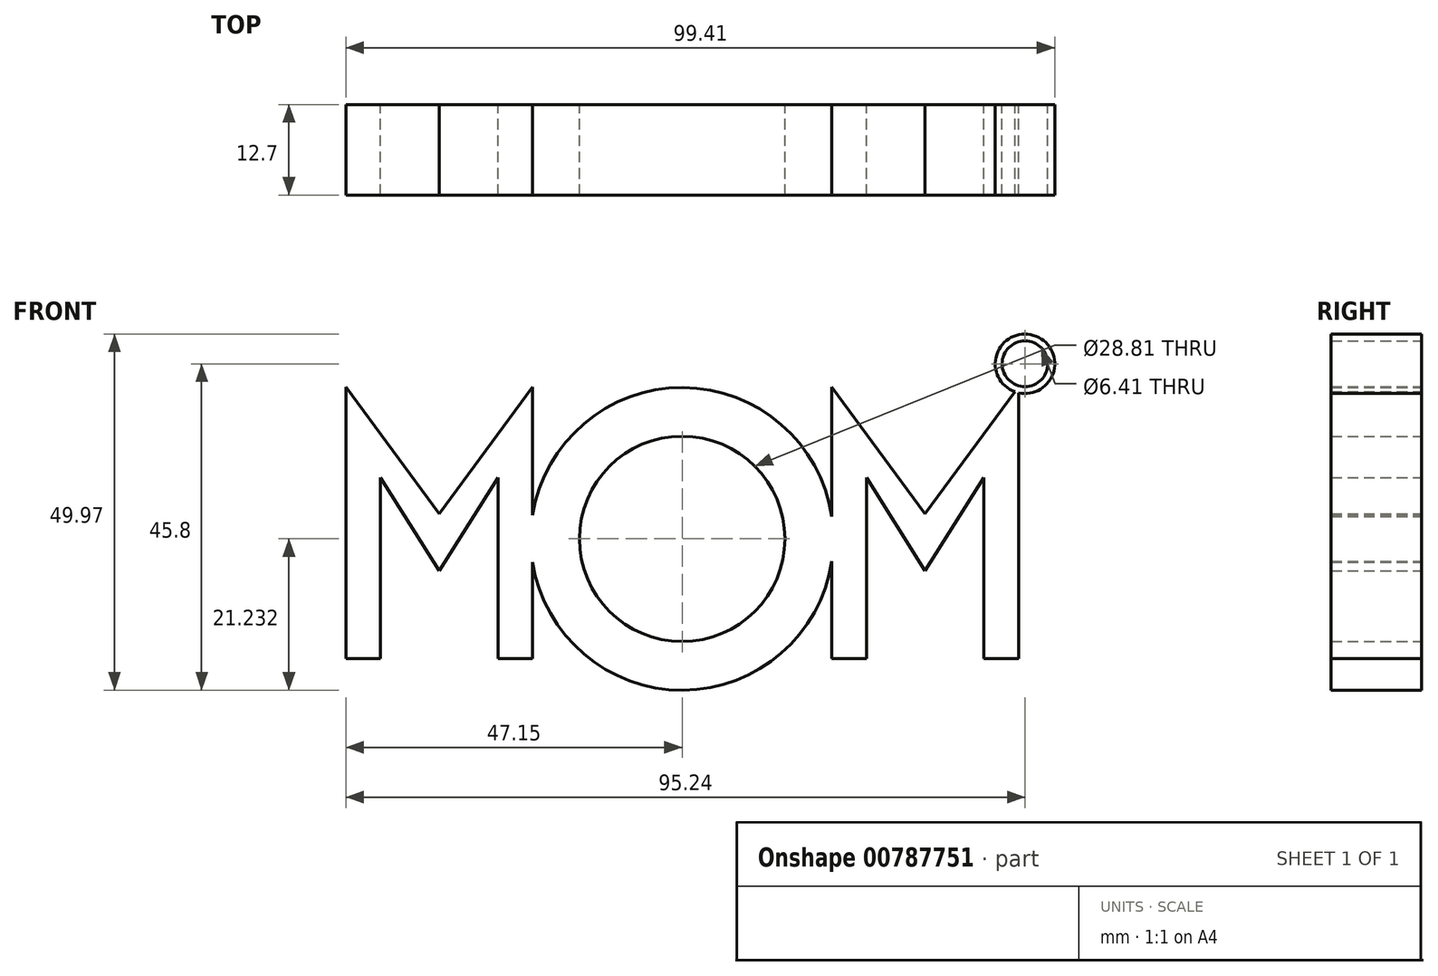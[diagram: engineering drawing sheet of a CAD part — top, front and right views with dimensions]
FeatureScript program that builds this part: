
annotation { "Feature Type Name" : "Feature", "Feature Type Description" : "" }
export const myFeature = defineFeature(function(context is Context, id is Id, definition is map)
    precondition{}
    {
        {
            var Q0;
            Q0=qCreatedBy(makeId("Front.planeOp"),FACE);
            var sketch = newSketch(context, id + "F0", { "sketchPlane" : qUnion([Q0])});
            skLineSegment(sketch, "E0", {"start": v(-42.31, -9.94) * mm, "end": v(-42.31, 15.46) * mm});
            skLineSegment(sketch, "E1", {"start": v(-42.31, 15.46) * mm, "end": v(-34.06, 2.34) * mm});
            skLineSegment(sketch, "E2", {"start": v(-34.06, 2.34) * mm, "end": v(-25.81, 15.46) * mm});
            skLineSegment(sketch, "E3", {"start": v(-25.81, 15.46) * mm, "end": v(-25.81, -9.94) * mm});
            skLineSegment(sketch, "E4", {"start": v(-42.31, -9.94) * mm, "end": v(-47.15, -9.94) * mm});
            skLineSegment(sketch, "E5", {"start": v(-47.15, -9.94) * mm, "end": v(-47.15, 28.16) * mm});
            skLineSegment(sketch, "E6", {"start": v(-47.15, 28.16) * mm, "end": v(-34.06, 10.35) * mm});
            skLineSegment(sketch, "E7", {"start": v(-34.06, 10.35) * mm, "end": v(-20.97, 28.16) * mm});
            skLineSegment(sketch, "E8", {"start": v(-20.97, 28.16) * mm, "end": v(-20.97, -9.94) * mm});
            skLineSegment(sketch, "E9", {"start": v(-20.97, -9.94) * mm, "end": v(-25.81, -9.94) * mm});
            skCircle(sketch, "E10", {"center": v(0, 6.83) * mm, "radius": 21.23 * mm});
            skCircle(sketch, "E11", {"center": v(0, 6.83) * mm, "radius": 14.4 * mm});
            skLineSegment(sketch, "E12", {"start": v(25.84, -9.94) * mm, "end": v(25.84, 15.46) * mm});
            skLineSegment(sketch, "E13", {"start": v(25.84, 15.46) * mm, "end": v(34.09, 2.34) * mm});
            skLineSegment(sketch, "E14", {"start": v(34.09, 2.34) * mm, "end": v(42.34, 15.46) * mm});
            skLineSegment(sketch, "E15", {"start": v(42.34, 15.46) * mm, "end": v(42.34, -9.94) * mm});
            skLineSegment(sketch, "E16", {"start": v(25.84, -9.94) * mm, "end": v(21, -9.94) * mm});
            skLineSegment(sketch, "E17", {"start": v(21, -9.94) * mm, "end": v(21, 28.16) * mm});
            skLineSegment(sketch, "E18", {"start": v(21, 28.16) * mm, "end": v(34.09, 10.35) * mm});
            skLineSegment(sketch, "E19", {"start": v(34.09, 10.35) * mm, "end": v(47.18, 28.16) * mm});
            skLineSegment(sketch, "E20", {"start": v(47.18, 28.16) * mm, "end": v(47.18, -9.94) * mm});
            skLineSegment(sketch, "E21", {"start": v(47.18, -9.94) * mm, "end": v(42.34, -9.94) * mm});
            skCircle(sketch, "E22", {"center": v(48.09, 31.4) * mm, "radius": 4.17 * mm});
            skCircle(sketch, "E23", {"center": v(48.09, 31.4) * mm, "radius": 3.2 * mm});
            skSolve(sketch);
        }
        {
            var Q0;
            Q0 = qSketchRegion(id + "F0", true);
            extrude(context, id + "F1", {"entities" : qUnion([Q0]), "endBound" : BoundingType.SYMMETRIC, "depth" : 12.7 * mm, "offsetDistance" : 25.4 * mm});
        }
    });
